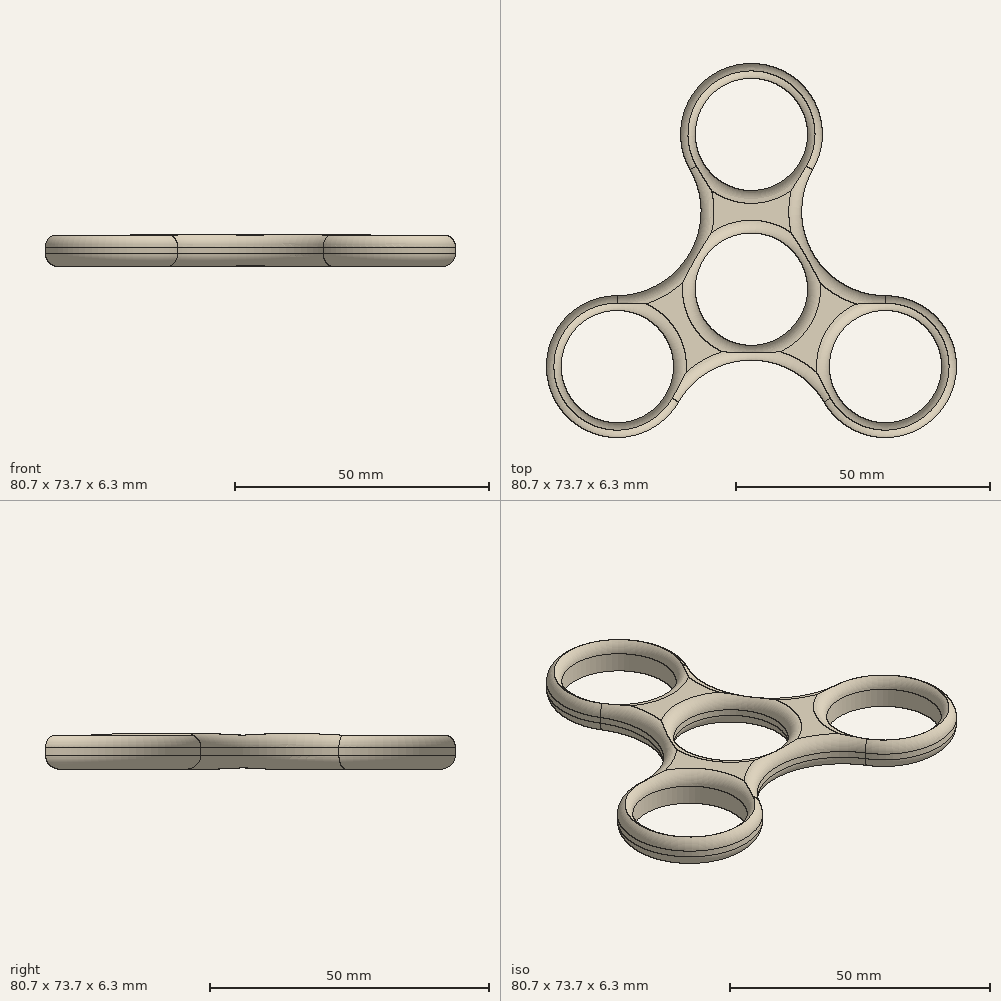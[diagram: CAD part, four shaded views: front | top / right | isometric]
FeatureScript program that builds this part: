
annotation { "Feature Type Name" : "Feature", "Feature Type Description" : "" }
export const myFeature = defineFeature(function(context is Context, id is Id, definition is map)
    precondition{}
    {
        {
            var Q0;
            Q0=qCreatedBy(makeId("Top.planeOp"),FACE);
            var sketch = newSketch(context, id + "F0", { "sketchPlane" : qUnion([Q0])});
            skCircle(sketch, "E0", {"center": v(0, 0) * mm, "radius": 11.05 * mm});
            skCircle(sketch, "E1", {"center": v(0, 0) * mm, "radius": 13.97 * mm});
            skCircle(sketch, "E2", {"center": v(0, 30.48) * mm, "radius": 11.05 * mm});
            skCircle(sketch, "E3", {"center": v(0, 30.48) * mm, "radius": 13.97 * mm});
            skCircle(sketch, "E4.1.0", {"center": v(-26.4, -15.24) * mm, "radius": 11.05 * mm});
            skCircle(sketch, "E4.2.0", {"center": v(26.4, -15.24) * mm, "radius": 11.05 * mm});
            skCircle(sketch, "E5.1.0", {"center": v(-26.4, -15.24) * mm, "radius": 13.97 * mm});
            skCircle(sketch, "E5.2.0", {"center": v(26.4, -15.24) * mm, "radius": 13.97 * mm});
            skArc(sketch, "E6", {"start": v(-26.4, -1.27) * mm, "mid": v(-12.1, 6.98) * mm, "end": v(-12.1, 23.5) * mm});
            skArc(sketch, "E7", {"start": v(-26.4, -1.27) * mm, "mid": v(-12.14, 7.01) * mm, "end": v(-12.1, 23.5) * mm});
            skArc(sketch, "E8.1.0", {"start": v(14.3, -22.23) * mm, "mid": v(0, -13.97) * mm, "end": v(-14.3, -22.22) * mm});
            skArc(sketch, "E8.2.0", {"start": v(12.1, 23.5) * mm, "mid": v(12.1, 6.98) * mm, "end": v(26.4, -1.27) * mm});
            skLineSegment(sketch, "E9.trimOffspring", {"start": v(-12.1, 6.98) * mm, "end": v(-12.14, 7.01) * mm});
            skSolve(sketch);
        }
        {
            var Q0;
            Q0 = qSketchRegion(id + "F0", true);
            extrude(context, id + "F1", {"entities" : qUnion([Q0]), "depth" : 6.35 * mm, "offsetDistance" : 25.4 * mm});
        }
        {
            var Q0;
            Q0=makeQuery(id+"F1.opExtrude","CAP_EDGE",EDGE,{"disambiguationData":[OSD([sQuery(id+"F0.wireOp",EDGE,"E8.1.0")])],"isStart":false});
            var Q1;
            Q1=makeQuery(id+"F1.opExtrude","CAP_EDGE",EDGE,{"disambiguationData":[OSD([sQuery(id+"F0.wireOp",EDGE,"E5.1.0")])],"isStart":false});
            var Q2;
            Q2=makeQuery(id+"F1.opExtrude","CAP_FACE",FACE,{"disambiguationData":[OSD([sQuery(id+"F0.wireOp",EDGE,"E0"),sQuery(id+"F0.wireOp",EDGE,"E2"),sQuery(id+"F0.wireOp",EDGE,"E3"),sQuery(id+"F0.wireOp",EDGE,"E4.1.0"),sQuery(id+"F0.wireOp",EDGE,"E4.2.0"),sQuery(id+"F0.wireOp",EDGE,"E5.1.0"),sQuery(id+"F0.wireOp",EDGE,"E5.2.0"),sQuery(id+"F0.wireOp",EDGE,"E7"),sQuery(id+"F0.wireOp",EDGE,"E8.1.0"),sQuery(id+"F0.wireOp",EDGE,"E8.2.0")])],"isStart":false});
            fillet(context, id + "F2", {"entities" : qUnion([Q0, Q1, Q2]), "radius" : 2.54 * mm, "tangentPropagation" : true, "allowEdgeOverflow" : false});
        }
        {
            var Q0;
            Q0=makeQuery(id+"F1.opExtrude","CAP_EDGE",EDGE,{"disambiguationData":[OSD([sQuery(id+"F0.wireOp",EDGE,"E8.1.0")])],"isStart":true});
            var Q1;
            Q1=makeQuery(id+"F1.opExtrude","CAP_EDGE",EDGE,{"disambiguationData":[OSD([sQuery(id+"F0.wireOp",EDGE,"E5.1.0")])],"isStart":true});
            var Q2;
            Q2=makeQuery(id+"F1.opExtrude","CAP_EDGE",EDGE,{"disambiguationData":[OSD([sQuery(id+"F0.wireOp",EDGE,"E7")])],"isStart":true});
            var Q3;
            Q3=makeQuery(id+"F1.opExtrude","CAP_EDGE",EDGE,{"disambiguationData":[OSD([sQuery(id+"F0.wireOp",EDGE,"E0")])],"isStart":true});
            var Q4;
            Q4=makeQuery(id+"F1.opExtrude","CAP_EDGE",EDGE,{"disambiguationData":[OSD([sQuery(id+"F0.wireOp",EDGE,"E8.2.0")])],"isStart":true});
            var Q5;
            Q5=makeQuery(id+"F1.opExtrude","CAP_EDGE",EDGE,{"disambiguationData":[OSD([sQuery(id+"F0.wireOp",EDGE,"E3")])],"isStart":true});
            var Q6;
            Q6=makeQuery(id+"F1.opExtrude","CAP_EDGE",EDGE,{"disambiguationData":[OSD([sQuery(id+"F0.wireOp",EDGE,"E5.2.0")])],"isStart":true});
            fillet(context, id + "F3", {"entities" : qUnion([Q0, Q1, Q2, Q3, Q4, Q5, Q6]), "radius" : 2.54 * mm, "tangentPropagation" : true, "allowEdgeOverflow" : false});
        }
    });
